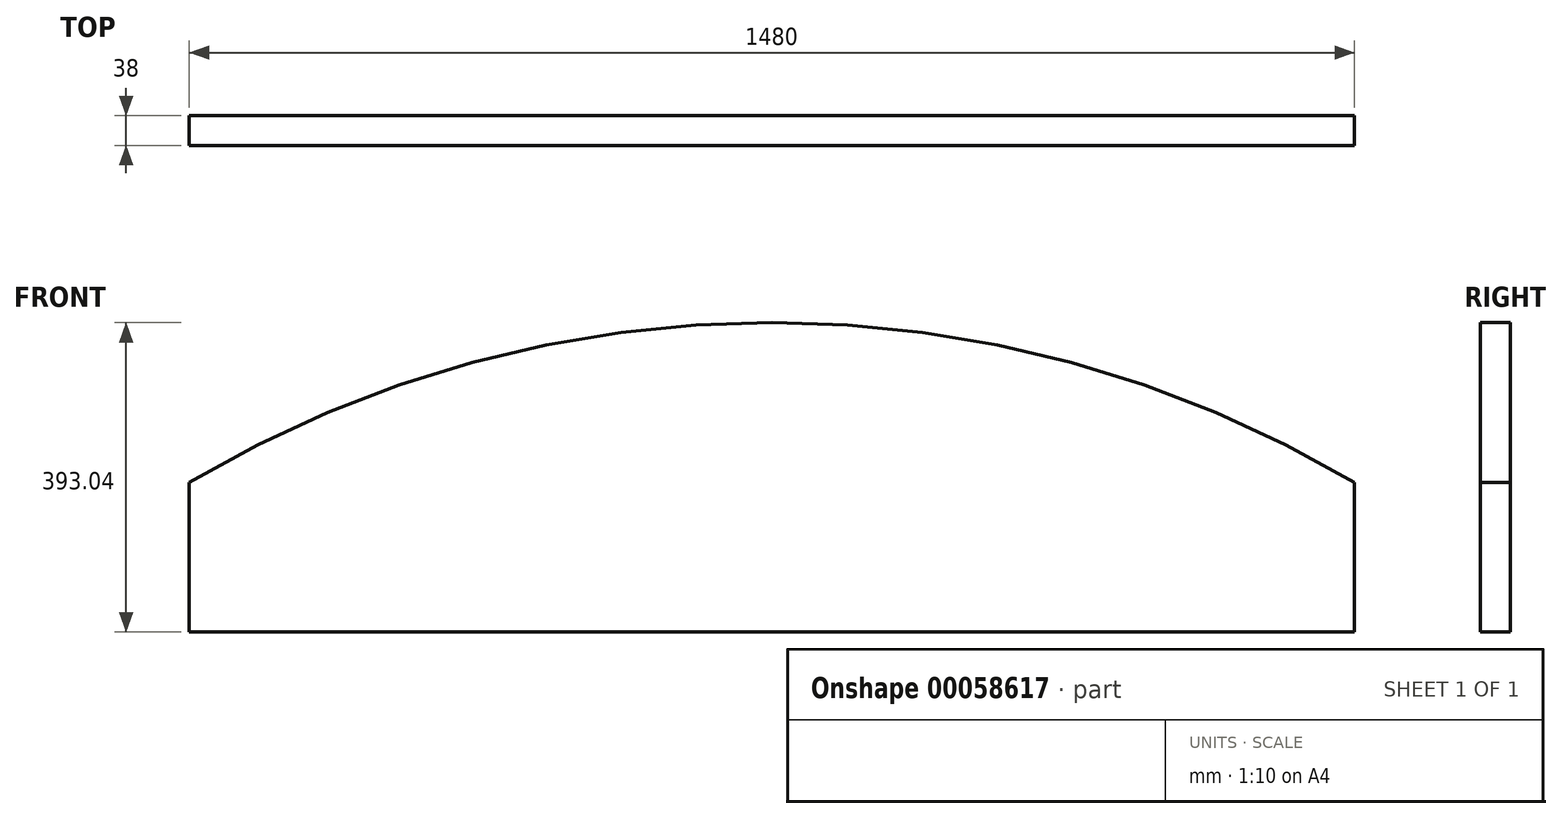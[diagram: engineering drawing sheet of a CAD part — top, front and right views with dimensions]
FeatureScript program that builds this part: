
annotation { "Feature Type Name" : "Feature", "Feature Type Description" : "" }
export const myFeature = defineFeature(function(context is Context, id is Id, definition is map)
    precondition{}
    {
        {
            var Q0;
            Q0=qCreatedBy(makeId("Front.planeOp"),FACE);
            var sketch = newSketch(context, id + "F0", { "sketchPlane" : qUnion([Q0])});
            skLineSegment(sketch, "E0", {"start": v(0, 0) * mm, "end": v(1480, 0) * mm});
            skLineSegment(sketch, "E1", {"start": v(1480, 0) * mm, "end": v(1480, 190) * mm});
            skLineSegment(sketch, "E2", {"start": v(0, 0) * mm, "end": v(0, 190) * mm});
            skArc(sketch, "E3", {"start": v(1480, 190) * mm, "mid": v(740, 393.04) * mm, "end": v(0, 190) * mm});
            skSolve(sketch);
        }
        {
            var Q0;
            Q0 = qSketchRegion(id + "F0", true);
            extrude(context, id + "F1", {"entities" : qUnion([Q0]), "depth" : 38 * mm});
        }
    });
